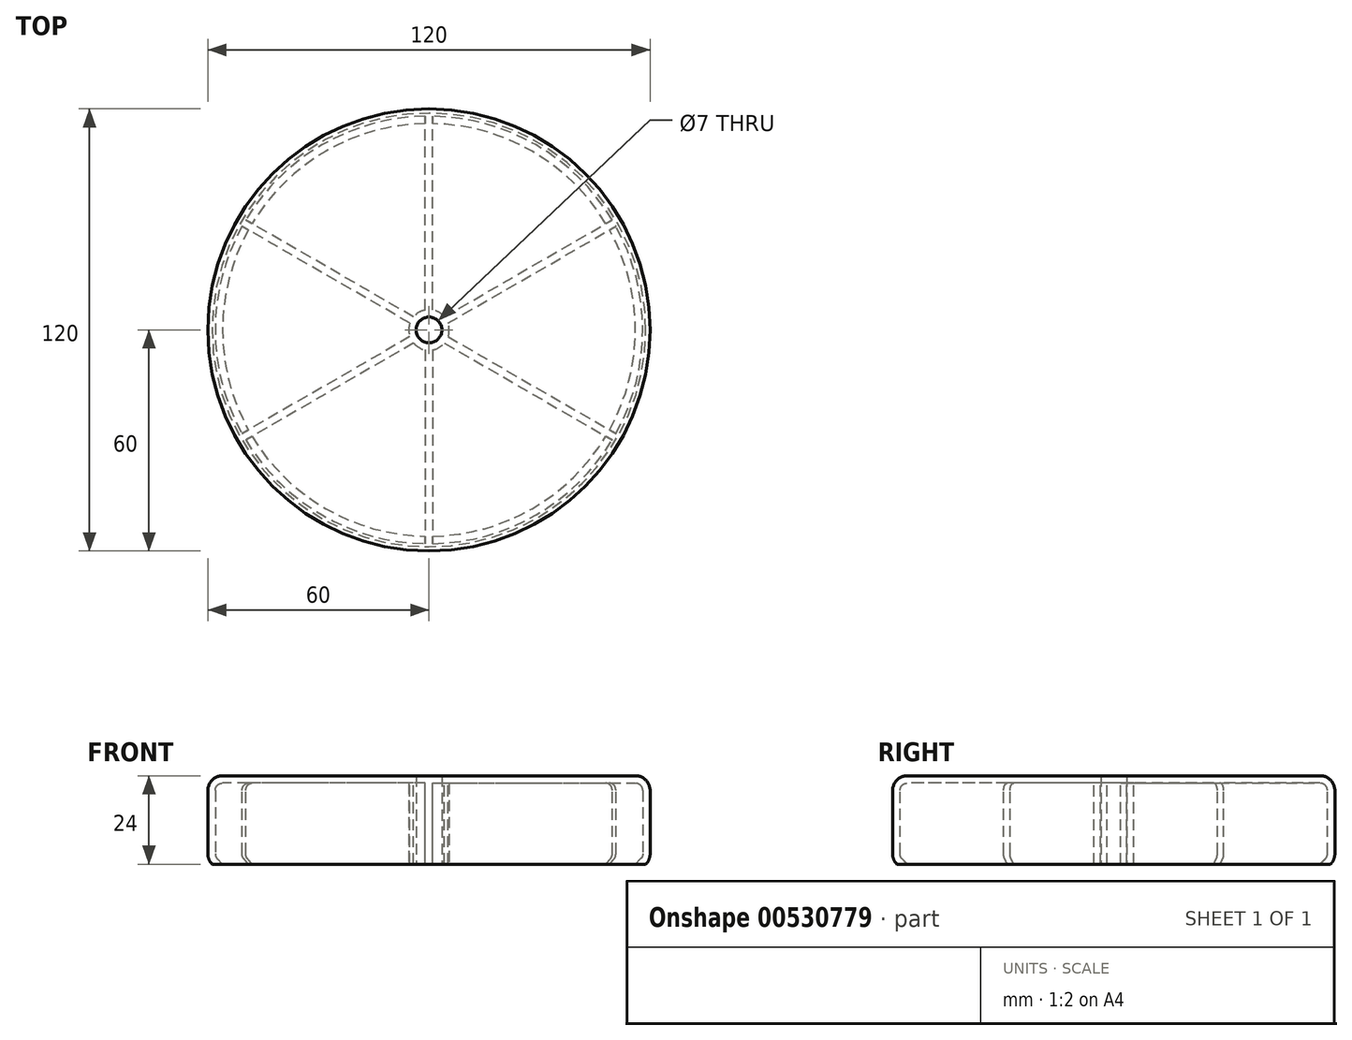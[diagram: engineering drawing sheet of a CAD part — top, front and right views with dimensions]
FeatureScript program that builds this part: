
annotation { "Feature Type Name" : "Feature", "Feature Type Description" : "" }
export const myFeature = defineFeature(function(context is Context, id is Id, definition is map)
    precondition{}
    {
        {
            var Q0;
            Q0=qCreatedBy(makeId("Front.planeOp"),FACE);
            var sketch = newSketch(context, id + "F0", { "sketchPlane" : qUnion([Q0])});
            skLineSegment(sketch, "E0", {"start": v(-56, 12) * mm, "end": v(-3.5, 12) * mm});
            skArc(sketch, "E1", {"start": v(-56, 12) * mm, "mid": v(-58.83, 10.83) * mm, "end": v(-60, 8) * mm});
            skArc(sketch, "E2", {"start": v(-56, 10) * mm, "mid": v(-57.41, 9.41) * mm, "end": v(-58, 8) * mm});
            skLineSegment(sketch, "E3", {"start": v(-56, 10) * mm, "end": v(-5.5, 10) * mm});
            skArc(sketch, "E4", {"start": v(-60, -9.17) * mm, "mid": v(-59.7, -10.7) * mm, "end": v(-58.83, -12) * mm});
            skArc(sketch, "E5", {"start": v(-58, -9.17) * mm, "mid": v(-57.85, -9.94) * mm, "end": v(-57.41, -10.59) * mm});
            skLineSegment(sketch, "E6", {"start": v(-56, -9.17) * mm, "end": v(-58.83, -12) * mm, "construction": true});
            skLineSegment(sketch, "E7", {"start": v(-60, 8) * mm, "end": v(-60, -9.17) * mm});
            skLineSegment(sketch, "E8", {"start": v(-58, 8) * mm, "end": v(-58, -9.17) * mm});
            skLineSegment(sketch, "E9", {"start": v(-57.41, -10.59) * mm, "end": v(-56, -12) * mm});
            skLineSegment(sketch, "E10", {"start": v(-56, -12) * mm, "end": v(-58.83, -12) * mm});
            skLineSegment(sketch, "E11", {"start": v(-5.5, 10) * mm, "end": v(-5.5, -12) * mm});
            skLineSegment(sketch, "E12", {"start": v(-5.5, -12) * mm, "end": v(-3.5, -12) * mm});
            skLineSegment(sketch, "E13", {"start": v(-3.5, -12) * mm, "end": v(-3.5, 12) * mm});
            skLineSegment(sketch, "E14", {"start": v(0, -12) * mm, "end": v(0, 12) * mm, "construction": true});
            skLineSegment(sketch, "E15", {"start": v(-60, 8) * mm, "end": v(-58, 8) * mm, "construction": true});
            skLineSegment(sketch, "E16.MirrorCS", {"start": v(3.5, -12) * mm, "end": v(3.5, 12) * mm});
            skLineSegment(sketch, "E17.MirrorCS", {"start": v(5.5, -12) * mm, "end": v(3.5, -12) * mm});
            skLineSegment(sketch, "E18.MirrorCS", {"start": v(5.5, 10) * mm, "end": v(5.5, -12) * mm});
            skLineSegment(sketch, "E19.MirrorCS", {"start": v(56, 10) * mm, "end": v(5.5, 10) * mm});
            skLineSegment(sketch, "E20.MirrorCS", {"start": v(56, 12) * mm, "end": v(3.5, 12) * mm});
            skArc(sketch, "E21.MirrorCS", {"start": v(56, 12) * mm, "mid": v(58.83, 10.83) * mm, "end": v(60, 8) * mm});
            skArc(sketch, "E22.MirrorCS", {"start": v(56, 10) * mm, "mid": v(57.41, 9.41) * mm, "end": v(58, 8) * mm});
            skLineSegment(sketch, "E23.MirrorCS", {"start": v(60, 8) * mm, "end": v(60, -9.17) * mm});
            skLineSegment(sketch, "E24.MirrorCS", {"start": v(58, 8) * mm, "end": v(58, -9.17) * mm});
            skArc(sketch, "E25.MirrorCS", {"start": v(60, -9.17) * mm, "mid": v(59.7, -10.7) * mm, "end": v(58.83, -12) * mm});
            skArc(sketch, "E26.MirrorCS", {"start": v(58, -9.17) * mm, "mid": v(57.85, -9.94) * mm, "end": v(57.41, -10.59) * mm});
            skLineSegment(sketch, "E27.MirrorCS", {"start": v(57.41, -10.59) * mm, "end": v(56, -12) * mm});
            skLineSegment(sketch, "E28.MirrorCS", {"start": v(56, -12) * mm, "end": v(58.83, -12) * mm});
            skLineSegment(sketch, "E29", {"start": v(-58, 8) * mm, "end": v(-56, 8) * mm, "construction": true});
            skSolve(sketch);
        }
        {
            var Q0;
            Q0=makeQuery(id+"F0.imprint","IMPRINT",FACE,{"disambiguationData":[TD([[makeQuery(id+"F0.imprint","IMPRINT",EDGE,{"derivedFrom":sQuery(id+"F0.wireOp",EDGE,"E0")}),-1.0]])]});
            var Q1;
            Q1=sQuery(id+"F0.wireOp",EDGE,"E14");
            revolve(context, id + "F1", {"entities" : qUnion([Q0]), "axis" : qUnion([Q1]), "revolveType" : RevolveType.FULL});
        }
        {
            var Q0;
            Q0=makeQuery(id+"F1.opRevolve","SWEPT_FACE",FACE,{"disambiguationData":[OSD([sQuery(id+"F0.wireOp",EDGE,"E3")])]});
            var sketch = newSketch(context, id + "F2", { "sketchPlane" : qUnion([Q0])});
            skLineSegment(sketch, "E30", {"start": v(0, 0) * mm, "end": v(0, -56) * mm, "construction": true});
            skLineSegment(sketch, "E31", {"start": v(-1, -5.4) * mm, "end": v(-1, -56) * mm});
            skLineSegment(sketch, "E32.MirrorCS", {"start": v(1, -5.4) * mm, "end": v(1, -56) * mm});
            skArc(sketch, "E33", {"start": v(-1, -5.4) * mm, "mid": v(0, -5.5) * mm, "end": v(1, -5.4) * mm});
            skLineSegment(sketch, "E34", {"start": v(-1, -56) * mm, "end": v(-1, -58) * mm});
            skLineSegment(sketch, "E35.MirrorCS", {"start": v(1, -56) * mm, "end": v(1, -58) * mm});
            skArc(sketch, "E36", {"start": v(-1, -58) * mm, "mid": v(0, -58) * mm, "end": v(1, -58) * mm});
            skSolve(sketch);
        }
        {
            var Q0;
            {var subQ0=sQuery(id+"F2.wireOp",EDGE,"E34");Q0=makeQuery(id+"F2.imprint","IMPRINT",FACE,{"disambiguationData":[TD([[makeQuery(id+"F2.imprint","IMPRINT",EDGE,{"derivedFrom":subQ0}),1.0]])]});}
            var Q1;
            {var subQ0=sQuery(id+"F2.wireOp",EDGE,"E31");Q1=makeQuery(id+"F2.imprint","IMPRINT",FACE,{"disambiguationData":[TD([[makeQuery(id+"F2.imprint","IMPRINT",EDGE,{"derivedFrom":subQ0}),1.0]])]});}
            var Q2;
            Q2=makeQuery(id+"F1.opRevolve","SWEPT_FACE",FACE,{"disambiguationData":[OSD([sQuery(id+"F0.wireOp",EDGE,"E10")])]});
            extrude(context, id + "F3", {"entities" : qUnion([Q0, Q1]), "endBound" : BoundingType.UP_TO_SURFACE, "depth" : 25 * mm, "endBoundEntityFace" : qUnion([Q2]), "offsetDistance" : 25 * mm});
        }
        {
            var Q0;
            Q0=makeQuery(id+"F3.opExtrude","SWEPT_BODY",BODY,{"disambiguationData":[OSD([sQuery(id+"F2.wireOp",EDGE,"E31"),sQuery(id+"F2.wireOp",EDGE,"E32.MirrorCS"),sQuery(id+"F2.wireOp",EDGE,"E33"),sQuery(id+"F2.wireOp",EDGE,"E34"),sQuery(id+"F2.wireOp",EDGE,"E35.MirrorCS"),sQuery(id+"F2.wireOp",EDGE,"E36")])]});
            var Q1;
            Q1=sQuery(id+"F0.wireOp",EDGE,"E14");
            var Q2;
            Q2=makeQuery(id+"F1.opRevolve","SWEPT_BODY",BODY,{"disambiguationData":[OSD([sQuery(id+"F0.wireOp",EDGE,"E0"),sQuery(id+"F0.wireOp",EDGE,"E1"),sQuery(id+"F0.wireOp",EDGE,"E2"),sQuery(id+"F0.wireOp",EDGE,"E3"),sQuery(id+"F0.wireOp",EDGE,"E4"),sQuery(id+"F0.wireOp",EDGE,"E5"),sQuery(id+"F0.wireOp",EDGE,"E7"),sQuery(id+"F0.wireOp",EDGE,"E8"),sQuery(id+"F0.wireOp",EDGE,"E9"),sQuery(id+"F0.wireOp",EDGE,"E10"),sQuery(id+"F0.wireOp",EDGE,"E11"),sQuery(id+"F0.wireOp",EDGE,"E12"),sQuery(id+"F0.wireOp",EDGE,"E13")])]});
            circularPattern(context, id + "F4", {"operationType" : NewBodyOperationType.ADD, "entities" : qUnion([Q0]), "axis" : qUnion([Q1]), "angle" : 360 * degree, "instanceCount" : 6, "equalSpace" : true});
        }
    });
